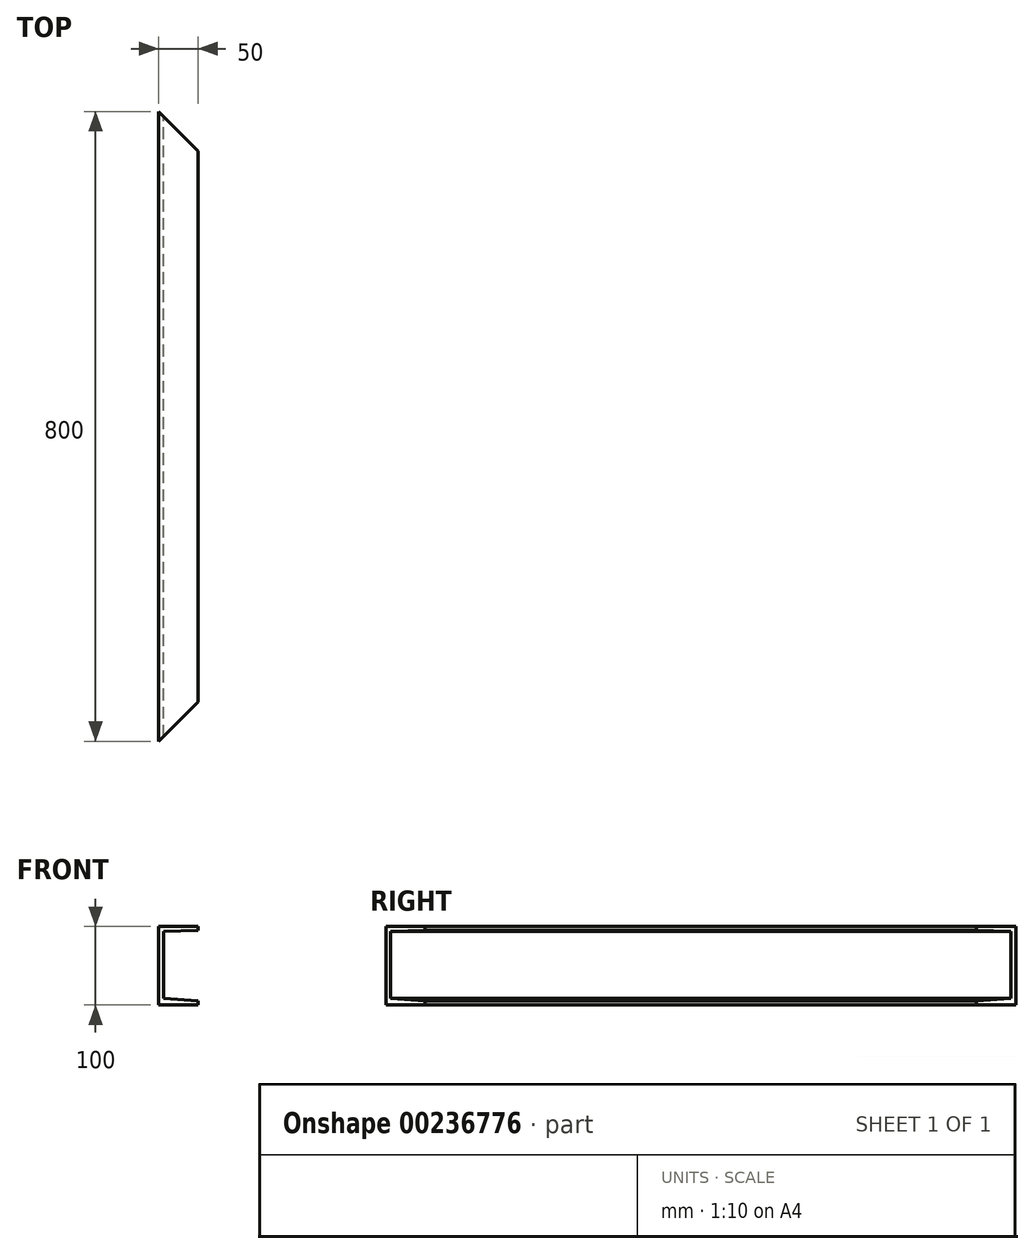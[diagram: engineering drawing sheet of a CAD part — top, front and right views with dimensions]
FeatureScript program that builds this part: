
annotation { "Feature Type Name" : "Feature", "Feature Type Description" : "" }
export const myFeature = defineFeature(function(context is Context, id is Id, definition is map)
    precondition{}
    {
        {
            var Q0;
            Q0=qCreatedBy(makeId("Front.planeOp"),FACE);
            var sketch = newSketch(context, id + "F0", { "sketchPlane" : qUnion([Q0])});
            skLineSegment(sketch, "E0.bottom", {"start": v(0, 0) * mm, "end": v(50, 0) * mm});
            skLineSegment(sketch, "E0.top", {"start": v(0, 100) * mm, "end": v(50, 100) * mm});
            skLineSegment(sketch, "E0.left", {"start": v(0, 0) * mm, "end": v(0, 100) * mm});
            skLineSegment(sketch, "E0.right", {"start": v(50, 0) * mm, "end": v(50, 5) * mm});
            skLineSegment(sketch, "E1.left", {"start": v(4.68, 71.03) * mm, "end": v(4.68, 71.03) * mm});
            skLineSegment(sketch, "E1.right", {"start": v(12.2, 71.03) * mm, "end": v(12.2, 71.03) * mm});
            skLineSegment(sketch, "E2", {"start": v(6, 8.46) * mm, "end": v(50, 5) * mm});
            skLineSegment(sketch, "E3", {"start": v(6, 8.46) * mm, "end": v(6, 93.46) * mm});
            skLineSegment(sketch, "E4", {"start": v(6, 93.46) * mm, "end": v(50, 95) * mm});
            skLineSegment(sketch, "E5.trimOffspring", {"start": v(50, 95) * mm, "end": v(50, 100) * mm});
            skSolve(sketch);
        }
        {
            var Q0;
            Q0=makeQuery(id+"F0.imprint","IMPRINT",FACE,{"disambiguationData":[TD([[makeQuery(id+"F0.imprint","IMPRINT",EDGE,{"derivedFrom":sQuery(id+"F0.wireOp",EDGE,"E0.bottom")}),1.0]])]});
            extrude(context, id + "F1", {"entities" : qUnion([Q0]), "depth" : 800 * mm, "offsetDistance" : 25 * mm});
        }
        {
            var Q0;
            Q0=qCreatedBy(makeId("Top.planeOp"),FACE);
            var sketch = newSketch(context, id + "F2", { "sketchPlane" : qUnion([Q0])});
            skLineSegment(sketch, "E6", {"start": v(0, 52.26) * mm, "end": v(87.16, 52.26) * mm});
            skLineSegment(sketch, "E7", {"start": v(87.16, 52.26) * mm, "end": v(87.16, -87.16) * mm});
            skLineSegment(sketch, "E8", {"start": v(87.16, -87.16) * mm, "end": v(0, 0) * mm});
            skLineSegment(sketch, "E9", {"start": v(0, 0) * mm, "end": v(0, 52.26) * mm});
            skPoint(sketch, "E10.orphan", {"position": v(-38.59, 52.26) * mm});
            skLineSegment(sketch, "E11", {"start": v(0, -810) * mm, "end": v(0, -800) * mm});
            skLineSegment(sketch, "E12", {"start": v(0, -800) * mm, "end": v(98.87, -701.13) * mm});
            skLineSegment(sketch, "E13", {"start": v(98.87, -701.13) * mm, "end": v(98.87, -810) * mm});
            skLineSegment(sketch, "E14", {"start": v(98.87, -810) * mm, "end": v(0, -810) * mm});
            skSolve(sketch);
        }
        {
            var Q0;
            Q0 = qSketchRegion(id + "F2", true);
            var Q1;
            Q1=makeQuery(id+"F1.opExtrude","SWEPT_FACE",FACE,{"disambiguationData":[OSD([sQuery(id+"F0.wireOp",EDGE,"E0.top")])]});
            extrude(context, id + "F3", {"entities" : qUnion([Q0, Q1]), "operationType" : NewBodyOperationType.REMOVE, "depth" : 110 * mm, "offsetDistance" : 25 * mm});
        }
    });
